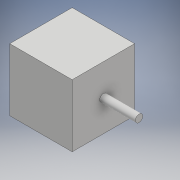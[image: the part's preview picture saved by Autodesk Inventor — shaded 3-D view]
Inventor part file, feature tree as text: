
AUTODESK INVENTOR PART (.ipt)
format: ipt  version: 2017 (Build 210142000, 142)  size: 95,744 bytes
history: native  units: mm
features: extrude x2, sketch x2
ambient origin geometry x8: Origin, YZ Plane, XZ Plane, XY Plane, X Axis, Y Axis, Z Axis, Center Point
bodies: Solid1 (feature_tree)
feature tree (4):
  extrude  "Extrusion1"  Depth=42.0mm
  extrude  "Extrusion2"  Depth=24.0mm
  sketch  "Sketch1"  dims[d0=42.0mm d1=42.0mm]
  sketch  "Sketch2"  dims[d2=42.0mm d3=0.0mm d4=5.0mm d5=24.0mm d6=0.0mm]
